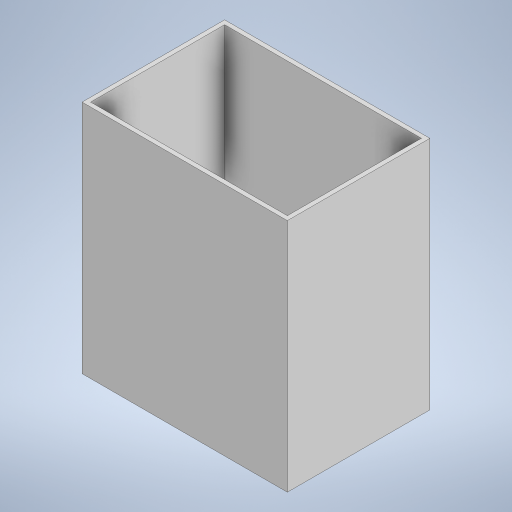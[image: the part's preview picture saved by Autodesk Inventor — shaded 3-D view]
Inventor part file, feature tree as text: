
AUTODESK INVENTOR PART (.ipt)
format: ipt  version: 2024 (Build 280153000, 153)  size: 193,536 bytes
history: native  units: mm
features: extrude x2, sketch x2
ambient origin geometry x8: Origin, YZ Plane, XZ Plane, XY Plane, X Axis, Y Axis, Z Axis, Center Point
bodies: Body1 (feature_tree)
feature tree (4):
  extrude  "Extrusión2"  Depth=50.0mm
  extrude  "Extrusión3"  Depth=1.5mm
  sketch  "Boceto3"  dims[d8=72.0mm d9=50.0mm]
  sketch  "Boceto5"  dims[d10=82.5mm d11=0.0mm d12=1.5mm d13=1.5mm d14=1.5mm d15=1.5mm d16=81.0mm d17=0.0mm]
